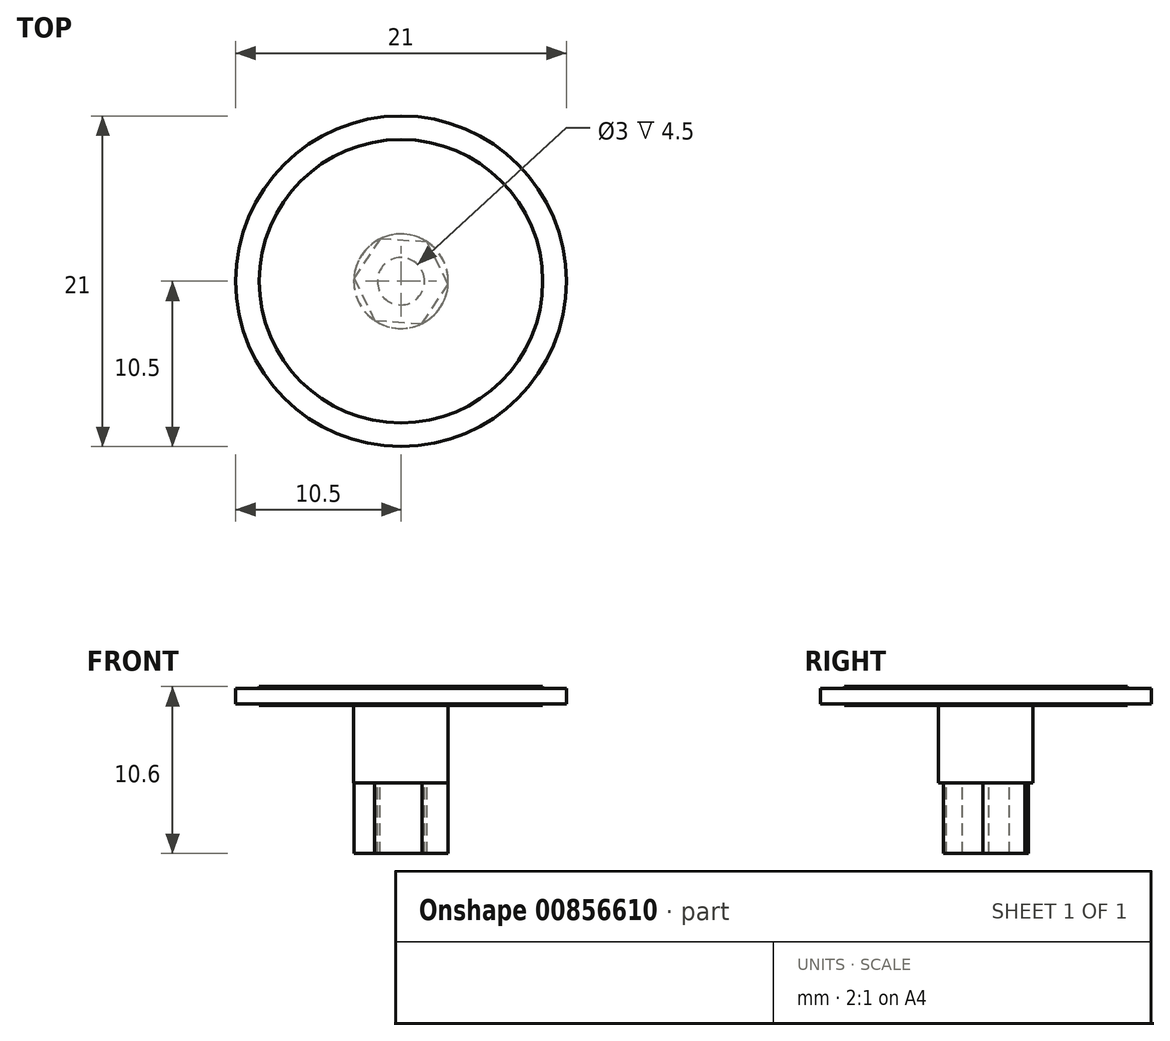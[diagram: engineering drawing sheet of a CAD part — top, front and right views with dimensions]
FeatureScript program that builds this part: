
annotation { "Feature Type Name" : "Feature", "Feature Type Description" : "" }
export const myFeature = defineFeature(function(context is Context, id is Id, definition is map)
    precondition{}
    {
        {
            var Q0;
            Q0=qCreatedBy(makeId("Top.planeOp"),FACE);
            var sketch = newSketch(context, id + "F0", { "sketchPlane" : qUnion([Q0])});
            skCircle(sketch, "E0", {"center": v(0, 0) * mm, "radius": 10.5 * mm});
            skCircle(sketch, "E1", {"center": v(0, 0) * mm, "radius": 3 * mm});
            skCircle(sketch, "E2", {"center": v(0, 0) * mm, "radius": 9 * mm});
            skSolve(sketch);
        }
        {
            var Q0;
            Q0=makeQuery(id+"F0.imprint","IMPRINT",FACE,{"disambiguationData":[TD([[makeQuery(id+"F0.imprint","IMPRINT",EDGE,{"derivedFrom":sQuery(id+"F0.wireOp",EDGE,"E1")}),-1.0]])]});
            var Q1;
            Q1=makeQuery(id+"F0.imprint","IMPRINT",FACE,{"disambiguationData":[TD([[makeQuery(id+"F0.imprint","IMPRINT",EDGE,{"derivedFrom":sQuery(id+"F0.wireOp",EDGE,"E0")}),1.0]])]});
            var Q2;
            Q2=makeQuery(id+"F0.imprint","IMPRINT",FACE,{"disambiguationData":[TD([[makeQuery(id+"F0.imprint","IMPRINT",EDGE,{"derivedFrom":sQuery(id+"F0.wireOp",EDGE,"E1")}),1.0]])]});
            extrude(context, id + "F1", {"entities" : qUnion([Q0, Q1, Q2]), "depth" : 1 * mm, "offsetDistance" : 25 * mm});
        }
        {
            var Q0;
            Q0=makeQuery(id+"F0.imprint","IMPRINT",FACE,{"disambiguationData":[TD([[makeQuery(id+"F0.imprint","IMPRINT",EDGE,{"derivedFrom":sQuery(id+"F0.wireOp",EDGE,"E1")}),1.0]])]});
            extrude(context, id + "F2", {"entities" : qUnion([Q0]), "operationType" : NewBodyOperationType.ADD, "oppositeDirection" : true, "depth" : 5 * mm, "offsetDistance" : 25 * mm});
        }
        {
            var Q0;
            Q0=makeQuery(id+"F0.imprint","IMPRINT",FACE,{"disambiguationData":[TD([[makeQuery(id+"F0.imprint","IMPRINT",EDGE,{"derivedFrom":sQuery(id+"F0.wireOp",EDGE,"E1")}),-1.0]])]});
            extrude(context, id + "F3", {"entities" : qUnion([Q0]), "operationType" : NewBodyOperationType.ADD, "depth" : 0.1 * mm, "offsetDistance" : 25 * mm});
        }
        {
            var Q0;
            Q0=makeQuery(id+"F0.imprint","IMPRINT",FACE,{"disambiguationData":[TD([[makeQuery(id+"F0.imprint","IMPRINT",EDGE,{"derivedFrom":sQuery(id+"F0.wireOp",EDGE,"E1")}),-1.0]])]});
            extrude(context, id + "F4", {"entities" : qUnion([Q0]), "operationType" : NewBodyOperationType.ADD, "oppositeDirection" : true, "depth" : 0.1 * mm, "offsetDistance" : 25 * mm});
        }
        {
            var Q0;
            Q0=makeQuery(id+"F1.opExtrude","CAP_FACE",FACE,{"disambiguationData":[OSD([sQuery(id+"F0.wireOp",EDGE,"E0")])],"isStart":false});
            var sketch = newSketch(context, id + "F5", { "sketchPlane" : qUnion([Q0])});
            skCircle(sketch, "E3", {"center": v(0, 0) * mm, "radius": 9 * mm});
            skSolve(sketch);
        }
        {
            var Q0;
            Q0=makeQuery(id+"F5.imprint","IMPRINT",FACE,{"disambiguationData":[TD([[makeQuery(id+"F5.imprint","IMPRINT",EDGE,{"derivedFrom":sQuery(id+"F5.wireOp",EDGE,"E3")}),1.0]])]});
            extrude(context, id + "F6", {"entities" : qUnion([Q0]), "operationType" : NewBodyOperationType.ADD, "depth" : 0.1 * mm, "offsetDistance" : 25 * mm});
        }
        {
            var Q0;
            Q0=makeQuery(id+"F2.opExtrude","CAP_FACE",FACE,{"disambiguationData":[OSD([sQuery(id+"F0.wireOp",EDGE,"E1")])],"isStart":false});
            var sketch = newSketch(context, id + "F7", { "sketchPlane" : qUnion([Q0])});
            skCircle(sketch, "E4", {"center": v(0, 0) * mm, "radius": 1.5 * mm});
            skCircle(sketch, "E5.cCircle", {"center": v(0, 0) * mm, "radius": 2.6 * mm, "construction": true});
            skLineSegment(sketch, "E5.0", {"start": v(3, 0.2) * mm, "end": v(1.67, -2.5) * mm});
            skLineSegment(sketch, "E5.1", {"start": v(1.67, -2.5) * mm, "end": v(-1.33, -2.7) * mm});
            skLineSegment(sketch, "E5.2", {"start": v(-1.33, -2.7) * mm, "end": v(-3, -0.2) * mm});
            skLineSegment(sketch, "E5.3", {"start": v(-3, -0.2) * mm, "end": v(-1.67, 2.5) * mm});
            skLineSegment(sketch, "E5.4", {"start": v(-1.67, 2.5) * mm, "end": v(1.33, 2.7) * mm});
            skLineSegment(sketch, "E5.5", {"start": v(1.33, 2.7) * mm, "end": v(3, 0.2) * mm});
            skPoint(sketch, "E5.0.midPoint", {"position": v(2.33, -1.15) * mm});
            skPoint(sketch, "E6", {"position": v(3, 0.2) * mm});
            skPoint(sketch, "E7", {"position": v(1.67, -2.5) * mm});
            skPoint(sketch, "E8", {"position": v(-1.33, -2.7) * mm});
            skPoint(sketch, "E9", {"position": v(-3, -0.2) * mm});
            skPoint(sketch, "E10", {"position": v(-1.67, 2.5) * mm});
            skPoint(sketch, "E11", {"position": v(1.33, 2.7) * mm});
            skSolve(sketch);
        }
        {
            var Q0;
            Q0=makeQuery(id+"F7.imprint","IMPRINT",FACE,{"disambiguationData":[TD([[makeQuery(id+"F7.imprint","IMPRINT",EDGE,{"derivedFrom":sQuery(id+"F7.wireOp",EDGE,"E4")}),-1.0]])]});
            extrude(context, id + "F8", {"entities" : qUnion([Q0]), "operationType" : NewBodyOperationType.ADD, "depth" : 4.5 * mm, "offsetDistance" : 25 * mm});
        }
    });
